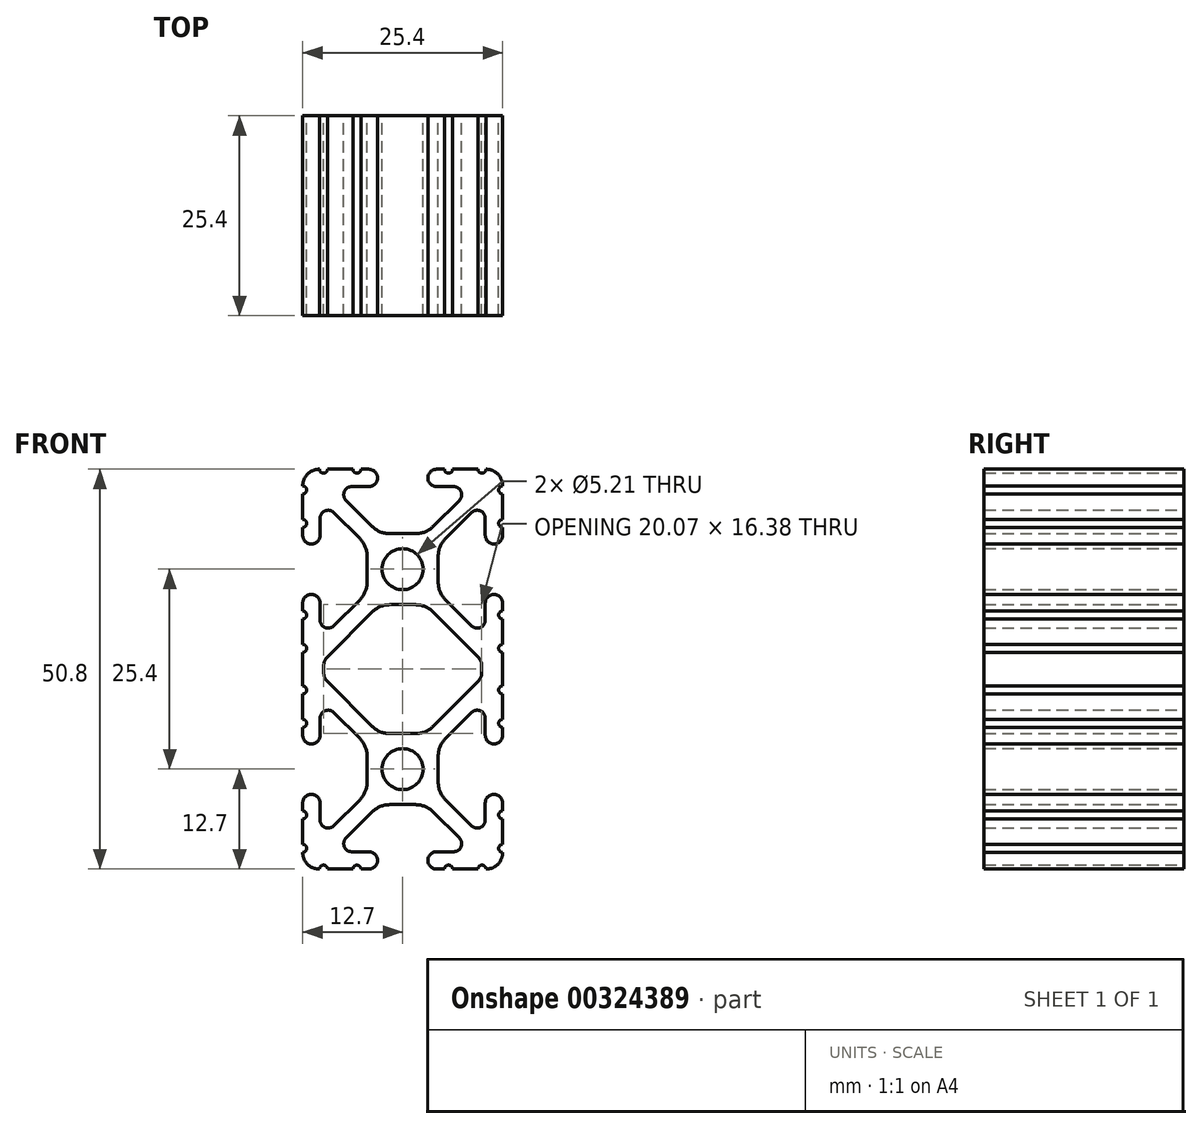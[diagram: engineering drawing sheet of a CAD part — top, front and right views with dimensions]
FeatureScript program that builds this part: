
annotation { "Feature Type Name" : "Feature", "Feature Type Description" : "" }
export const myFeature = defineFeature(function(context is Context, id is Id, definition is map)
    precondition{}
    {
        {
            var Q0;
            Q0=qCreatedBy(makeId("Front.planeOp"),FACE);
            var sketch = newSketch(context, id + "F0", { "sketchPlane" : qUnion([Q0])});
            skArc(sketch, "E0", {"start": v(2.6, -12.7) * mm, "mid": v(0, -10.1) * mm, "end": v(-2.6, -12.7) * mm});
            skArc(sketch, "E1", {"start": v(-2.6, -12.7) * mm, "mid": v(0, -15.3) * mm, "end": v(2.6, -12.7) * mm});
            skArc(sketch, "E2", {"start": v(-12.7, 22.25) * mm, "mid": v(-12.2, 22.76) * mm, "end": v(-12.7, 23.28) * mm});
            skLineSegment(sketch, "E3", {"start": v(-12.7, 22.25) * mm, "end": v(-12.7, 19.02) * mm});
            skArc(sketch, "E4", {"start": v(-12.7, 18) * mm, "mid": v(-12.2, 18.52) * mm, "end": v(-12.7, 19.02) * mm});
            skLineSegment(sketch, "E5", {"start": v(-12.7, 18) * mm, "end": v(-12.7, 17) * mm});
            skArc(sketch, "E6", {"start": v(-12.7, 17) * mm, "mid": v(-11.6, 15.9) * mm, "end": v(-10.5, 17) * mm});
            skLineSegment(sketch, "E7", {"start": v(-10.5, 17) * mm, "end": v(-10.5, 19.17) * mm});
            skArc(sketch, "E8", {"start": v(-8.76, 19.9) * mm, "mid": v(-9.86, 20.11) * mm, "end": v(-10.5, 19.17) * mm});
            skLineSegment(sketch, "E9", {"start": v(-8.76, 19.9) * mm, "end": v(-5.44, 16.58) * mm});
            skArc(sketch, "E10", {"start": v(-4.5, 14.33) * mm, "mid": v(-4.75, 15.55) * mm, "end": v(-5.44, 16.58) * mm});
            skLineSegment(sketch, "E11", {"start": v(-4.5, 14.33) * mm, "end": v(-4.5, 11.07) * mm});
            skArc(sketch, "E12", {"start": v(-5.44, 8.82) * mm, "mid": v(-4.75, 9.85) * mm, "end": v(-4.5, 11.07) * mm});
            skLineSegment(sketch, "E13", {"start": v(-5.44, 8.82) * mm, "end": v(-8.76, 5.5) * mm});
            skArc(sketch, "E14", {"start": v(-10.5, 6.23) * mm, "mid": v(-9.86, 5.29) * mm, "end": v(-8.76, 5.5) * mm});
            skLineSegment(sketch, "E15", {"start": v(-10.5, 6.23) * mm, "end": v(-10.5, 8.4) * mm});
            skArc(sketch, "E16", {"start": v(-10.5, 8.4) * mm, "mid": v(-11.6, 9.5) * mm, "end": v(-12.7, 8.4) * mm});
            skLineSegment(sketch, "E17", {"start": v(-12.7, 8.4) * mm, "end": v(-12.7, 7.4) * mm});
            skArc(sketch, "E18", {"start": v(-12.7, 6.38) * mm, "mid": v(-12.2, 6.88) * mm, "end": v(-12.7, 7.4) * mm});
            skLineSegment(sketch, "E19", {"start": v(-12.7, 6.38) * mm, "end": v(-12.7, 3.15) * mm});
            skArc(sketch, "E20", {"start": v(-12.7, 2.13) * mm, "mid": v(-12.2, 2.64) * mm, "end": v(-12.7, 3.15) * mm});
            skLineSegment(sketch, "E21", {"start": v(-12.7, 2.13) * mm, "end": v(-12.7, -2.13) * mm});
            skArc(sketch, "E22", {"start": v(-12.7, -3.15) * mm, "mid": v(-12.2, -2.64) * mm, "end": v(-12.7, -2.13) * mm});
            skLineSegment(sketch, "E23", {"start": v(-12.7, -3.15) * mm, "end": v(-12.7, -6.38) * mm});
            skArc(sketch, "E24", {"start": v(-12.7, -7.4) * mm, "mid": v(-12.2, -6.88) * mm, "end": v(-12.7, -6.38) * mm});
            skLineSegment(sketch, "E25", {"start": v(-12.7, -7.4) * mm, "end": v(-12.7, -8.4) * mm});
            skArc(sketch, "E26", {"start": v(-12.7, -8.4) * mm, "mid": v(-11.6, -9.5) * mm, "end": v(-10.5, -8.4) * mm});
            skLineSegment(sketch, "E27", {"start": v(-10.5, -8.4) * mm, "end": v(-10.5, -6.23) * mm});
            skArc(sketch, "E28", {"start": v(-8.76, -5.5) * mm, "mid": v(-9.86, -5.29) * mm, "end": v(-10.5, -6.23) * mm});
            skLineSegment(sketch, "E29", {"start": v(-8.76, -5.5) * mm, "end": v(-5.44, -8.82) * mm});
            skArc(sketch, "E30", {"start": v(-4.5, -11.07) * mm, "mid": v(-4.75, -9.85) * mm, "end": v(-5.44, -8.82) * mm});
            skLineSegment(sketch, "E31", {"start": v(-4.5, -11.07) * mm, "end": v(-4.5, -14.33) * mm});
            skArc(sketch, "E32", {"start": v(-5.44, -16.58) * mm, "mid": v(-4.75, -15.55) * mm, "end": v(-4.5, -14.33) * mm});
            skLineSegment(sketch, "E33", {"start": v(-5.44, -16.58) * mm, "end": v(-8.76, -19.9) * mm});
            skArc(sketch, "E34", {"start": v(-10.5, -19.17) * mm, "mid": v(-9.86, -20.11) * mm, "end": v(-8.76, -19.9) * mm});
            skLineSegment(sketch, "E35", {"start": v(-10.5, -19.17) * mm, "end": v(-10.5, -17) * mm});
            skArc(sketch, "E36", {"start": v(-10.5, -17) * mm, "mid": v(-11.6, -15.9) * mm, "end": v(-12.7, -17) * mm});
            skLineSegment(sketch, "E37", {"start": v(-12.7, -17) * mm, "end": v(-12.7, -18) * mm});
            skArc(sketch, "E38", {"start": v(-12.7, -19.02) * mm, "mid": v(-12.2, -18.52) * mm, "end": v(-12.7, -18) * mm});
            skLineSegment(sketch, "E39", {"start": v(-12.7, -19.02) * mm, "end": v(-12.7, -22.25) * mm});
            skArc(sketch, "E40", {"start": v(-12.7, -23.28) * mm, "mid": v(-12.2, -22.76) * mm, "end": v(-12.7, -22.25) * mm});
            skArc(sketch, "E41", {"start": v(-12.7, -23.28) * mm, "mid": v(-12.08, -24.78) * mm, "end": v(-10.58, -25.4) * mm});
            skArc(sketch, "E42", {"start": v(-9.55, -25.4) * mm, "mid": v(-10.06, -24.9) * mm, "end": v(-10.58, -25.4) * mm});
            skLineSegment(sketch, "E43", {"start": v(-9.55, -25.4) * mm, "end": v(-6.32, -25.4) * mm});
            skArc(sketch, "E44", {"start": v(-5.3, -25.4) * mm, "mid": v(-5.82, -24.9) * mm, "end": v(-6.32, -25.4) * mm});
            skLineSegment(sketch, "E45", {"start": v(-5.3, -25.4) * mm, "end": v(-4.3, -25.4) * mm});
            skArc(sketch, "E46", {"start": v(-4.3, -25.4) * mm, "mid": v(-3.2, -24.3) * mm, "end": v(-4.3, -23.2) * mm});
            skLineSegment(sketch, "E47", {"start": v(-4.3, -23.2) * mm, "end": v(-6.47, -23.2) * mm});
            skArc(sketch, "E48", {"start": v(-7.2, -21.46) * mm, "mid": v(-7.41, -22.56) * mm, "end": v(-6.47, -23.2) * mm});
            skLineSegment(sketch, "E49", {"start": v(-7.2, -21.46) * mm, "end": v(-3.88, -18.14) * mm});
            skArc(sketch, "E50", {"start": v(-1.63, -17.2) * mm, "mid": v(-2.85, -17.45) * mm, "end": v(-3.88, -18.14) * mm});
            skLineSegment(sketch, "E51", {"start": v(-1.63, -17.2) * mm, "end": v(1.63, -17.2) * mm});
            skArc(sketch, "E52", {"start": v(3.88, -18.14) * mm, "mid": v(2.85, -17.45) * mm, "end": v(1.63, -17.2) * mm});
            skLineSegment(sketch, "E53", {"start": v(3.88, -18.14) * mm, "end": v(7.2, -21.46) * mm});
            skArc(sketch, "E54", {"start": v(6.47, -23.2) * mm, "mid": v(7.41, -22.56) * mm, "end": v(7.2, -21.46) * mm});
            skLineSegment(sketch, "E55", {"start": v(6.47, -23.2) * mm, "end": v(4.3, -23.2) * mm});
            skArc(sketch, "E56", {"start": v(4.3, -23.2) * mm, "mid": v(3.2, -24.3) * mm, "end": v(4.3, -25.4) * mm});
            skLineSegment(sketch, "E57", {"start": v(4.3, -25.4) * mm, "end": v(5.3, -25.4) * mm});
            skArc(sketch, "E58", {"start": v(6.32, -25.4) * mm, "mid": v(5.82, -24.9) * mm, "end": v(5.3, -25.4) * mm});
            skLineSegment(sketch, "E59", {"start": v(6.32, -25.4) * mm, "end": v(9.55, -25.4) * mm});
            skArc(sketch, "E60", {"start": v(10.58, -25.4) * mm, "mid": v(10.06, -24.9) * mm, "end": v(9.55, -25.4) * mm});
            skArc(sketch, "E61", {"start": v(10.58, -25.4) * mm, "mid": v(12.08, -24.78) * mm, "end": v(12.7, -23.28) * mm});
            skArc(sketch, "E62", {"start": v(12.7, -22.25) * mm, "mid": v(12.2, -22.76) * mm, "end": v(12.7, -23.28) * mm});
            skLineSegment(sketch, "E63", {"start": v(12.7, -22.25) * mm, "end": v(12.7, -19.02) * mm});
            skArc(sketch, "E64", {"start": v(12.7, -18) * mm, "mid": v(12.2, -18.52) * mm, "end": v(12.7, -19.02) * mm});
            skLineSegment(sketch, "E65", {"start": v(12.7, -18) * mm, "end": v(12.7, -17) * mm});
            skArc(sketch, "E66", {"start": v(12.7, -17) * mm, "mid": v(11.6, -15.9) * mm, "end": v(10.5, -17) * mm});
            skLineSegment(sketch, "E67", {"start": v(10.5, -17) * mm, "end": v(10.5, -19.17) * mm});
            skArc(sketch, "E68", {"start": v(8.76, -19.9) * mm, "mid": v(9.86, -20.11) * mm, "end": v(10.5, -19.17) * mm});
            skLineSegment(sketch, "E69", {"start": v(8.76, -19.9) * mm, "end": v(5.44, -16.58) * mm});
            skArc(sketch, "E70", {"start": v(4.5, -14.33) * mm, "mid": v(4.75, -15.55) * mm, "end": v(5.44, -16.58) * mm});
            skLineSegment(sketch, "E71", {"start": v(4.5, -14.33) * mm, "end": v(4.5, -11.07) * mm});
            skArc(sketch, "E72", {"start": v(5.44, -8.82) * mm, "mid": v(4.75, -9.85) * mm, "end": v(4.5, -11.07) * mm});
            skLineSegment(sketch, "E73", {"start": v(5.44, -8.82) * mm, "end": v(8.76, -5.5) * mm});
            skArc(sketch, "E74", {"start": v(10.5, -6.23) * mm, "mid": v(9.86, -5.29) * mm, "end": v(8.76, -5.5) * mm});
            skLineSegment(sketch, "E75", {"start": v(10.5, -6.23) * mm, "end": v(10.5, -8.4) * mm});
            skArc(sketch, "E76", {"start": v(10.5, -8.4) * mm, "mid": v(11.6, -9.5) * mm, "end": v(12.7, -8.4) * mm});
            skLineSegment(sketch, "E77", {"start": v(12.7, -8.4) * mm, "end": v(12.7, -7.4) * mm});
            skArc(sketch, "E78", {"start": v(12.7, -6.38) * mm, "mid": v(12.2, -6.88) * mm, "end": v(12.7, -7.4) * mm});
            skLineSegment(sketch, "E79", {"start": v(12.7, -6.38) * mm, "end": v(12.7, -3.15) * mm});
            skArc(sketch, "E80", {"start": v(12.7, -2.13) * mm, "mid": v(12.2, -2.64) * mm, "end": v(12.7, -3.15) * mm});
            skLineSegment(sketch, "E81", {"start": v(12.7, -2.13) * mm, "end": v(12.7, 2.13) * mm});
            skArc(sketch, "E82", {"start": v(12.7, 3.15) * mm, "mid": v(12.2, 2.64) * mm, "end": v(12.7, 2.13) * mm});
            skLineSegment(sketch, "E83", {"start": v(12.7, 3.15) * mm, "end": v(12.7, 6.38) * mm});
            skArc(sketch, "E84", {"start": v(12.7, 7.4) * mm, "mid": v(12.2, 6.88) * mm, "end": v(12.7, 6.38) * mm});
            skLineSegment(sketch, "E85", {"start": v(12.7, 7.4) * mm, "end": v(12.7, 8.4) * mm});
            skArc(sketch, "E86", {"start": v(12.7, 8.4) * mm, "mid": v(11.6, 9.5) * mm, "end": v(10.5, 8.4) * mm});
            skLineSegment(sketch, "E87", {"start": v(10.5, 8.4) * mm, "end": v(10.5, 6.23) * mm});
            skArc(sketch, "E88", {"start": v(8.76, 5.5) * mm, "mid": v(9.86, 5.29) * mm, "end": v(10.5, 6.23) * mm});
            skLineSegment(sketch, "E89", {"start": v(8.76, 5.5) * mm, "end": v(5.44, 8.82) * mm});
            skArc(sketch, "E90", {"start": v(4.5, 11.07) * mm, "mid": v(4.75, 9.85) * mm, "end": v(5.44, 8.82) * mm});
            skLineSegment(sketch, "E91", {"start": v(4.5, 11.07) * mm, "end": v(4.5, 14.33) * mm});
            skArc(sketch, "E92", {"start": v(5.44, 16.58) * mm, "mid": v(4.75, 15.55) * mm, "end": v(4.5, 14.33) * mm});
            skLineSegment(sketch, "E93", {"start": v(5.44, 16.58) * mm, "end": v(8.76, 19.9) * mm});
            skArc(sketch, "E94", {"start": v(10.5, 19.17) * mm, "mid": v(9.86, 20.11) * mm, "end": v(8.76, 19.9) * mm});
            skLineSegment(sketch, "E95", {"start": v(10.5, 19.17) * mm, "end": v(10.5, 17) * mm});
            skArc(sketch, "E96", {"start": v(10.5, 17) * mm, "mid": v(11.6, 15.9) * mm, "end": v(12.7, 17) * mm});
            skLineSegment(sketch, "E97", {"start": v(12.7, 17) * mm, "end": v(12.7, 18) * mm});
            skArc(sketch, "E98", {"start": v(12.7, 19.02) * mm, "mid": v(12.2, 18.52) * mm, "end": v(12.7, 18) * mm});
            skLineSegment(sketch, "E99", {"start": v(12.7, 19.02) * mm, "end": v(12.7, 22.25) * mm});
            skArc(sketch, "E100", {"start": v(12.7, 23.28) * mm, "mid": v(12.2, 22.76) * mm, "end": v(12.7, 22.25) * mm});
            skArc(sketch, "E101", {"start": v(12.7, 23.28) * mm, "mid": v(12.08, 24.78) * mm, "end": v(10.58, 25.4) * mm});
            skArc(sketch, "E102", {"start": v(9.55, 25.4) * mm, "mid": v(10.06, 24.9) * mm, "end": v(10.58, 25.4) * mm});
            skLineSegment(sketch, "E103", {"start": v(9.55, 25.4) * mm, "end": v(6.32, 25.4) * mm});
            skArc(sketch, "E104", {"start": v(5.3, 25.4) * mm, "mid": v(5.82, 24.9) * mm, "end": v(6.32, 25.4) * mm});
            skLineSegment(sketch, "E105", {"start": v(5.3, 25.4) * mm, "end": v(4.3, 25.4) * mm});
            skArc(sketch, "E106", {"start": v(4.3, 25.4) * mm, "mid": v(3.2, 24.3) * mm, "end": v(4.3, 23.2) * mm});
            skLineSegment(sketch, "E107", {"start": v(4.3, 23.2) * mm, "end": v(6.47, 23.2) * mm});
            skArc(sketch, "E108", {"start": v(7.2, 21.46) * mm, "mid": v(7.41, 22.56) * mm, "end": v(6.47, 23.2) * mm});
            skLineSegment(sketch, "E109", {"start": v(7.2, 21.46) * mm, "end": v(3.88, 18.14) * mm});
            skArc(sketch, "E110", {"start": v(1.63, 17.2) * mm, "mid": v(2.85, 17.45) * mm, "end": v(3.88, 18.14) * mm});
            skLineSegment(sketch, "E111", {"start": v(1.63, 17.2) * mm, "end": v(-1.63, 17.2) * mm});
            skArc(sketch, "E112", {"start": v(-3.88, 18.14) * mm, "mid": v(-2.85, 17.45) * mm, "end": v(-1.63, 17.2) * mm});
            skLineSegment(sketch, "E113", {"start": v(-3.88, 18.14) * mm, "end": v(-7.2, 21.46) * mm});
            skArc(sketch, "E114", {"start": v(-6.47, 23.2) * mm, "mid": v(-7.41, 22.56) * mm, "end": v(-7.2, 21.46) * mm});
            skLineSegment(sketch, "E115", {"start": v(-6.47, 23.2) * mm, "end": v(-4.3, 23.2) * mm});
            skArc(sketch, "E116", {"start": v(-4.3, 23.2) * mm, "mid": v(-3.2, 24.3) * mm, "end": v(-4.3, 25.4) * mm});
            skLineSegment(sketch, "E117", {"start": v(-4.3, 25.4) * mm, "end": v(-5.3, 25.4) * mm});
            skArc(sketch, "E118", {"start": v(-6.32, 25.4) * mm, "mid": v(-5.82, 24.9) * mm, "end": v(-5.3, 25.4) * mm});
            skLineSegment(sketch, "E119", {"start": v(-6.32, 25.4) * mm, "end": v(-9.55, 25.4) * mm});
            skArc(sketch, "E120", {"start": v(-10.58, 25.4) * mm, "mid": v(-10.06, 24.9) * mm, "end": v(-9.55, 25.4) * mm});
            skArc(sketch, "E121", {"start": v(-10.58, 25.4) * mm, "mid": v(-12.08, 24.78) * mm, "end": v(-12.7, 23.28) * mm});
            skArc(sketch, "E122", {"start": v(2.6, 12.7) * mm, "mid": v(0, 15.3) * mm, "end": v(-2.6, 12.7) * mm});
            skArc(sketch, "E123", {"start": v(-2.6, 12.7) * mm, "mid": v(0, 10.1) * mm, "end": v(2.6, 12.7) * mm});
            skArc(sketch, "E124", {"start": v(-9.57, 1.57) * mm, "mid": v(-9.91, 1.05) * mm, "end": v(-10.03, 0.45) * mm});
            skLineSegment(sketch, "E125", {"start": v(-3.88, 7.26) * mm, "end": v(-9.57, 1.57) * mm});
            skArc(sketch, "E126", {"start": v(-1.63, 8.2) * mm, "mid": v(-2.85, 7.95) * mm, "end": v(-3.88, 7.26) * mm});
            skLineSegment(sketch, "E127", {"start": v(1.63, 8.2) * mm, "end": v(-1.63, 8.2) * mm});
            skArc(sketch, "E128", {"start": v(3.88, 7.26) * mm, "mid": v(2.85, 7.95) * mm, "end": v(1.63, 8.2) * mm});
            skLineSegment(sketch, "E129", {"start": v(9.57, 1.57) * mm, "end": v(3.88, 7.26) * mm});
            skArc(sketch, "E130", {"start": v(10.03, 0.45) * mm, "mid": v(9.91, 1.05) * mm, "end": v(9.57, 1.57) * mm});
            skLineSegment(sketch, "E131", {"start": v(10.03, -0.45) * mm, "end": v(10.03, 0.45) * mm});
            skArc(sketch, "E132", {"start": v(9.57, -1.57) * mm, "mid": v(9.91, -1.05) * mm, "end": v(10.03, -0.45) * mm});
            skLineSegment(sketch, "E133", {"start": v(3.88, -7.26) * mm, "end": v(9.57, -1.57) * mm});
            skArc(sketch, "E134", {"start": v(1.63, -8.2) * mm, "mid": v(2.85, -7.95) * mm, "end": v(3.88, -7.26) * mm});
            skLineSegment(sketch, "E135", {"start": v(-1.63, -8.2) * mm, "end": v(1.63, -8.2) * mm});
            skArc(sketch, "E136", {"start": v(-3.88, -7.26) * mm, "mid": v(-2.85, -7.95) * mm, "end": v(-1.63, -8.2) * mm});
            skLineSegment(sketch, "E137", {"start": v(-9.57, -1.57) * mm, "end": v(-3.88, -7.26) * mm});
            skArc(sketch, "E138", {"start": v(-10.03, -0.45) * mm, "mid": v(-9.91, -1.05) * mm, "end": v(-9.57, -1.57) * mm});
            skLineSegment(sketch, "E139", {"start": v(-10.03, 0.45) * mm, "end": v(-10.03, -0.45) * mm});
            skSolve(sketch);
        }
        {
            var Q0;
            Q0=makeQuery(id+"F0.imprint","IMPRINT",FACE,{"disambiguationData":[TD([[makeQuery(id+"F0.imprint","IMPRINT",EDGE,{"derivedFrom":sQuery(id+"F0.wireOp",EDGE,"E0")}),-1.0]])]});
            extrude(context, id + "F1", {"entities" : qUnion([Q0]), "depth" : 25.4 * mm});
        }
    });
